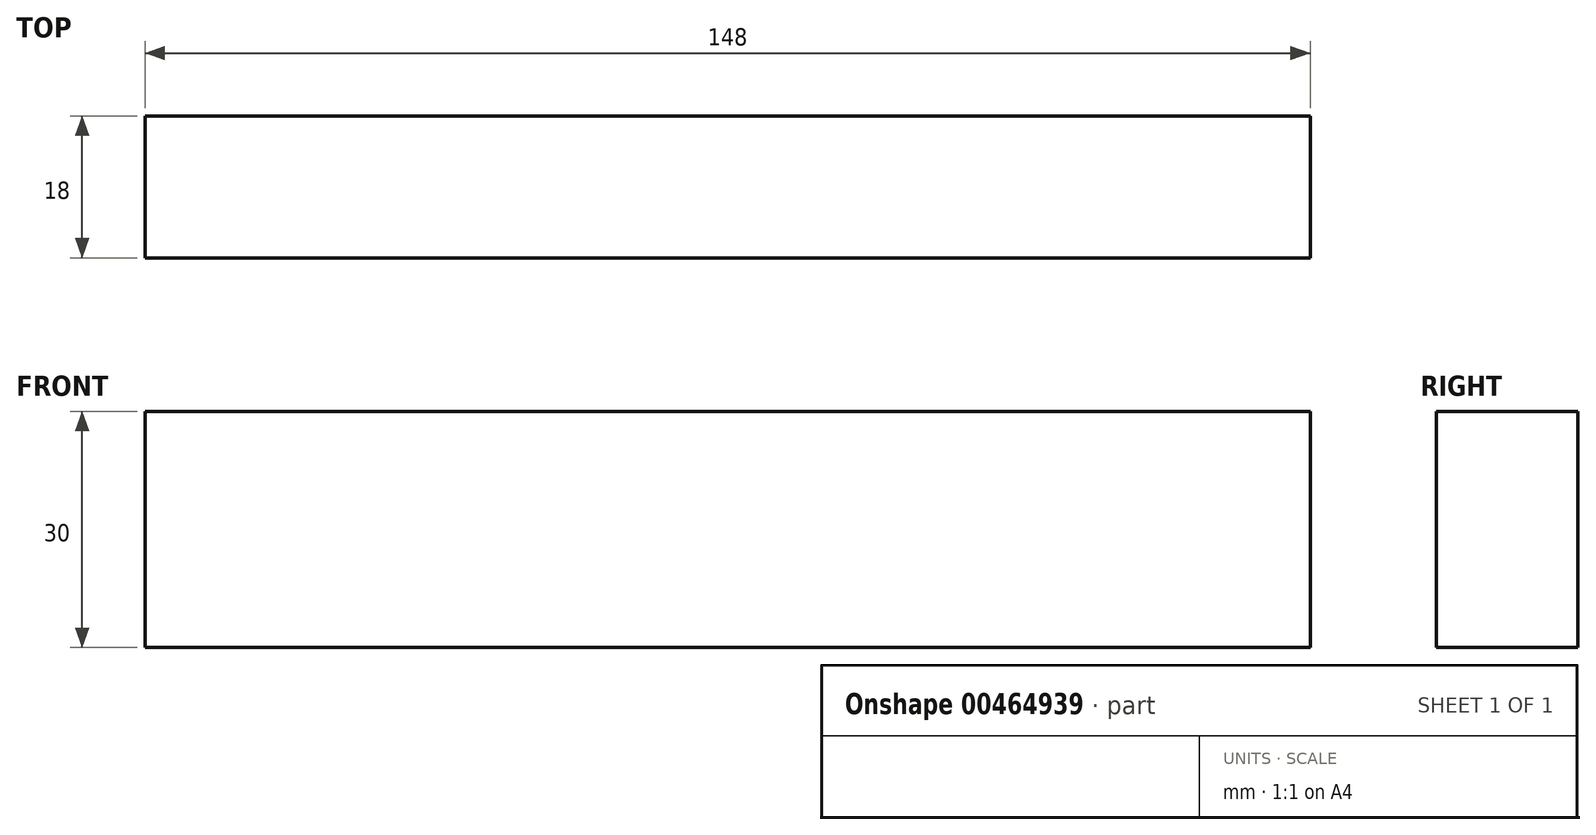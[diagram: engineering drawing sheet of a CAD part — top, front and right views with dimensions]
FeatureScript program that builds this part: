
annotation { "Feature Type Name" : "Feature", "Feature Type Description" : "" }
export const myFeature = defineFeature(function(context is Context, id is Id, definition is map)
    precondition{}
    {
        {
            var Q0;
            Q0=qCreatedBy(makeId("Right.planeOp"),FACE);
            var sketch = newSketch(context, id + "F0", { "sketchPlane" : qUnion([Q0])});
            skLineSegment(sketch, "E0.bottom", {"start": v(-9, 15) * mm, "end": v(9, 15) * mm});
            skLineSegment(sketch, "E0.top", {"start": v(-9, -15) * mm, "end": v(9, -15) * mm});
            skLineSegment(sketch, "E0.left", {"start": v(-9, 15) * mm, "end": v(-9, -15) * mm});
            skLineSegment(sketch, "E0.right", {"start": v(9, 15) * mm, "end": v(9, -15) * mm});
            skPoint(sketch, "E0.middle", {"position": v(0, 0) * mm});
            skSolve(sketch);
        }
        {
            var Q0;
            Q0=makeQuery(id+"F0.imprint","IMPRINT",FACE,{"disambiguationData":[TD([[makeQuery(id+"F0.imprint","IMPRINT",EDGE,{"derivedFrom":sQuery(id+"F0.wireOp",EDGE,"E0.bottom")}),-1.0]])]});
            extrude(context, id + "F1", {"entities" : qUnion([Q0]), "endBound" : BoundingType.SYMMETRIC, "depth" : (124 + 24) * mm, "offsetDistance" : 25 * mm});
        }
    });
